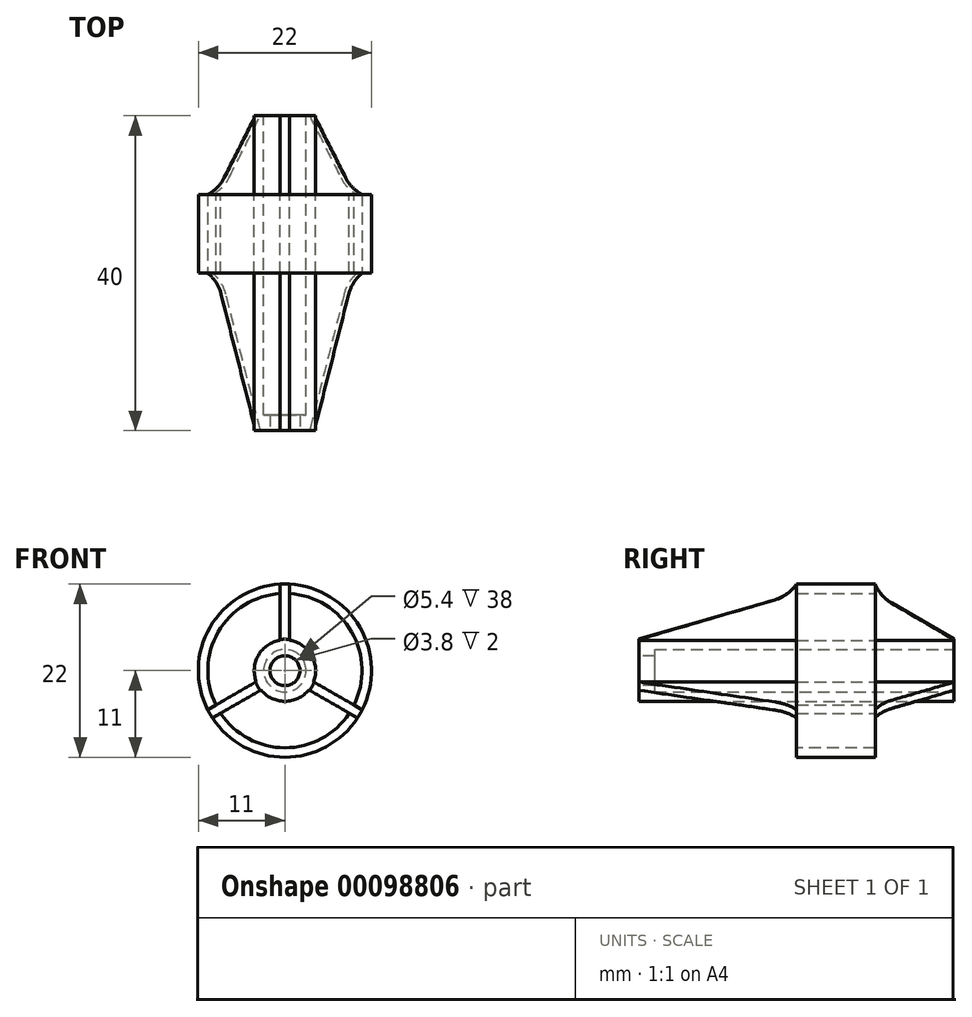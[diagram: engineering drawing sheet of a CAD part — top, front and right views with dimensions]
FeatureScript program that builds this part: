
annotation { "Feature Type Name" : "Feature", "Feature Type Description" : "" }
export const myFeature = defineFeature(function(context is Context, id is Id, definition is map)
    precondition{}
    {
        {
            var Q0;
            Q0=qCreatedBy(makeId("Front.planeOp"),FACE);
            var sketch = newSketch(context, id + "F0", { "sketchPlane" : qUnion([Q0])});
            skCircle(sketch, "E0", {"center": v(0, 0) * mm, "radius": 11 * mm});
            skCircle(sketch, "E1", {"center": v(0, 0) * mm, "radius": 9.8 * mm});
            skCircle(sketch, "E2", {"center": v(0, 0) * mm, "radius": 3.9 * mm});
            skCircle(sketch, "E3", {"center": v(0, 0) * mm, "radius": 2.7 * mm});
            skLineSegment(sketch, "E4", {"start": v(0, 3.9) * mm, "end": v(0, 9.8) * mm, "construction": true});
            skLineSegment(sketch, "E5", {"start": v(3.9, 0) * mm, "end": v(9.8, 0) * mm, "construction": true});
            skLineSegment(sketch, "E6", {"start": v(0, -3.9) * mm, "end": v(0, -9.8) * mm, "construction": true});
            skLineSegment(sketch, "E7", {"start": v(-3.9, 0) * mm, "end": v(-9.8, 0) * mm, "construction": true});
            skLineSegment(sketch, "E8", {"start": v(-0.6, 3.85) * mm, "end": v(-0.6, 9.78) * mm});
            skLineSegment(sketch, "E9", {"start": v(0.6, 9.78) * mm, "end": v(0.6, 3.85) * mm});
            skLineSegment(sketch, "E10.1.0", {"start": v(-8.77, -4.37) * mm, "end": v(-3.64, -1.4) * mm});
            skLineSegment(sketch, "E10.1.1", {"start": v(-3.04, -2.45) * mm, "end": v(-8.17, -5.41) * mm});
            skLineSegment(sketch, "E10.2.0", {"start": v(8.17, -5.41) * mm, "end": v(3.04, -2.45) * mm});
            skLineSegment(sketch, "E10.2.1", {"start": v(3.64, -1.4) * mm, "end": v(8.77, -4.37) * mm});
            skSolve(sketch);
        }
        {
            var Q0;
            Q0=makeQuery(id+"F0.imprint","IMPRINT",FACE,{"disambiguationData":[TD([[makeQuery(id+"F0.imprint","IMPRINT",EDGE,{"derivedFrom":sQuery(id+"F0.wireOp",EDGE,"E0")}),1.0]])]});
            extrude(context, id + "F1", {"entities" : qUnion([Q0]), "oppositeDirection" : true, "depth" : 10 * mm});
        }
        {
            var Q0;
            Q0=makeQuery(id+"F0.imprint","IMPRINT",FACE,{"disambiguationData":[TD([[makeQuery(id+"F0.imprint","IMPRINT",EDGE,{"derivedFrom":sQuery(id+"F0.wireOp",EDGE,"E2")}),1.0]])]});
            extrude(context, id + "F2", {"entities" : qUnion([Q0]), "operationType" : NewBodyOperationType.ADD, "depth" : 20 * mm, "hasSecondDirection" : true, "secondDirectionOppositeDirection" : true, "secondDirectionDepth" : 20 * mm});
        }
        {
            var Q0;
            {var subQ0=sQuery(id+"F0.wireOp",EDGE,"E8");Q0=makeQuery(id+"F0.imprint","IMPRINT",FACE,{"disambiguationData":[TD([[makeQuery(id+"F0.imprint","IMPRINT",EDGE,{"derivedFrom":subQ0}),-1.0]])]});}
            var Q1;
            {var subQ0=sQuery(id+"F0.wireOp",EDGE,"E10.2.0");Q1=makeQuery(id+"F0.imprint","IMPRINT",FACE,{"disambiguationData":[TD([[makeQuery(id+"F0.imprint","IMPRINT",EDGE,{"derivedFrom":subQ0}),-1.0]])]});}
            var Q2;
            {var subQ0=sQuery(id+"F0.wireOp",EDGE,"E10.1.0");Q2=makeQuery(id+"F0.imprint","IMPRINT",FACE,{"disambiguationData":[TD([[makeQuery(id+"F0.imprint","IMPRINT",EDGE,{"derivedFrom":subQ0}),-1.0]])]});}
            extrude(context, id + "F3", {"entities" : qUnion([Q0, Q1, Q2]), "operationType" : NewBodyOperationType.ADD, "depth" : 20 * mm, "hasSecondDirection" : true, "secondDirectionOppositeDirection" : true, "secondDirectionDepth" : 20 * mm});
        }
        {
            var Q0;
            {var subQ0=sQuery(id+"F0.wireOp",EDGE,"E2");var subQ1=sQuery(id+"F0.wireOp",EDGE,"E1");Q0=makeQuery(id+"F3.boolean.opBoolean","MERGE",FACE,{"derivedFrom":[makeQuery(id+"F2.opExtrude","CAP_FACE",FACE,{"disambiguationData":[OSD([subQ0,sQuery(id+"F0.wireOp",EDGE,"E3")])],"isStart":false}),makeQuery(id+"F3.opExtrude","CAP_FACE",FACE,{"disambiguationData":[OSD([subQ1,subQ0,sQuery(id+"F0.wireOp",EDGE,"d82addfd-7540-4472-8b44-bfc7bcca903d0.MirrorCS"),sQuery(id+"F0.wireOp",EDGE,"ad947069-a3ec-42d5-bcbd-703db36c13fa.trimOffspring")])],"isStart":false}),makeQuery(id+"F3.opExtrude","CAP_FACE",FACE,{"disambiguationData":[OSD([subQ1,subQ0,sQuery(id+"F0.wireOp",EDGE,"70a96751-7a45-4760-83c1-48eb2839d5d3.1.0"),sQuery(id+"F0.wireOp",EDGE,"70a96751-7a45-4760-83c1-48eb2839d5d3.1.1")])],"isStart":false}),makeQuery(id+"F3.opExtrude","CAP_FACE",FACE,{"disambiguationData":[OSD([subQ1,subQ0,sQuery(id+"F0.wireOp",EDGE,"70a96751-7a45-4760-83c1-48eb2839d5d3.2.0"),sQuery(id+"F0.wireOp",EDGE,"70a96751-7a45-4760-83c1-48eb2839d5d3.2.1")])],"isStart":false})]});}
            var sketch = newSketch(context, id + "F4", { "sketchPlane" : qUnion([Q0])});
            skCircle(sketch, "E11", {"center": v(0, 0) * mm, "radius": 1.9 * mm});
            skSolve(sketch);
        }
        {
            var Q0;
            Q0=makeQuery(id+"F4.imprint","IMPRINT",FACE,{"disambiguationData":[TD([[makeQuery(id+"F4.imprint","IMPRINT",EDGE,{"derivedFrom":sQuery(id+"F4.wireOp",EDGE,"E11")}),-1.0]])]});
            extrude(context, id + "F5", {"entities" : qUnion([Q0]), "operationType" : NewBodyOperationType.ADD, "oppositeDirection" : true, "depth" : 2 * mm});
        }
        {
            var Q0;
            {var subQ0=sQuery(id+"F0.wireOp",EDGE,"E1");Q0=makeQuery(id+"F3.opExtrude","CAP_EDGE",EDGE,{"disambiguationData":[OSD([subQ0]),TDD([makeQuery(id+"F0.imprint","IMPRINT",EDGE,{"disambiguationData":[TD([[makeQuery(id+"F0.imprint","INTERSECT",VERTEX,{"derivedFrom":[subQ0,sQuery(id+"F0.wireOp",EDGE,"E8")]}),1.0]])],"derivedFrom":subQ0})])],"isStart":false});}
            var Q1;
            {var subQ0=sQuery(id+"F0.wireOp",EDGE,"E1");Q1=makeQuery(id+"F3.opExtrude","CAP_EDGE",EDGE,{"disambiguationData":[OSD([subQ0]),TDD([makeQuery(id+"F0.imprint","IMPRINT",EDGE,{"disambiguationData":[TD([[makeQuery(id+"F0.imprint","INTERSECT",VERTEX,{"derivedFrom":[subQ0,sQuery(id+"F0.wireOp",EDGE,"E10.1.0")]}),-1.0]])],"derivedFrom":subQ0})])],"isStart":false});}
            var Q2;
            {var subQ0=sQuery(id+"F0.wireOp",EDGE,"E1");Q2=makeQuery(id+"F3.opExtrude","CAP_EDGE",EDGE,{"disambiguationData":[OSD([subQ0]),TDD([makeQuery(id+"F0.imprint","IMPRINT",EDGE,{"disambiguationData":[TD([[makeQuery(id+"F0.imprint","INTERSECT",VERTEX,{"derivedFrom":[subQ0,sQuery(id+"F0.wireOp",EDGE,"E10.2.0")]}),-1.0]])],"derivedFrom":subQ0})])],"isStart":false});}
            chamfer(context, id + "F6", {"entities" : qUnion([Q0, Q1, Q2]), "chamferType" : ChamferType.TWO_OFFSETS, "width1" : 5.8 * mm, "oppositeDirection" : false, "width2" : 20 * mm, "tangentPropagation" : true});
        }
        {
            var Q0;
            {var subQ0=sQuery(id+"F0.wireOp",EDGE,"E1");Q0=makeQuery(id+"F3.opExtrude","CAP_EDGE",EDGE,{"disambiguationData":[OSD([subQ0]),TDD([makeQuery(id+"F0.imprint","IMPRINT",EDGE,{"disambiguationData":[TD([[makeQuery(id+"F0.imprint","INTERSECT",VERTEX,{"derivedFrom":[subQ0,sQuery(id+"F0.wireOp",EDGE,"E10.2.0")]}),-1.0]])],"derivedFrom":subQ0})])],"isStart":true});}
            var Q1;
            {var subQ0=sQuery(id+"F0.wireOp",EDGE,"E1");Q1=makeQuery(id+"F3.opExtrude","CAP_EDGE",EDGE,{"disambiguationData":[OSD([subQ0]),TDD([makeQuery(id+"F0.imprint","IMPRINT",EDGE,{"disambiguationData":[TD([[makeQuery(id+"F0.imprint","INTERSECT",VERTEX,{"derivedFrom":[subQ0,sQuery(id+"F0.wireOp",EDGE,"E10.1.0")]}),-1.0]])],"derivedFrom":subQ0})])],"isStart":true});}
            var Q2;
            {var subQ0=sQuery(id+"F0.wireOp",EDGE,"E1");Q2=makeQuery(id+"F3.opExtrude","CAP_EDGE",EDGE,{"disambiguationData":[OSD([subQ0]),TDD([makeQuery(id+"F0.imprint","IMPRINT",EDGE,{"disambiguationData":[TD([[makeQuery(id+"F0.imprint","INTERSECT",VERTEX,{"derivedFrom":[subQ0,sQuery(id+"F0.wireOp",EDGE,"E8")]}),1.0]])],"derivedFrom":subQ0})])],"isStart":true});}
            chamfer(context, id + "F7", {"entities" : qUnion([Q0, Q1, Q2]), "chamferType" : ChamferType.TWO_OFFSETS, "width1" : 10 * mm, "oppositeDirection" : false, "width2" : 5.8 * mm, "tangentPropagation" : true});
        }
        {
            var Q0;
            {var subQ0=sQuery(id+"F0.wireOp",EDGE,"E1");Q0=makeQuery(id+"F6.opChamfer","BLEND_EDGE",EDGE,{"blendedFrom":[makeQuery(id+"F3.opExtrude","CAP_EDGE",EDGE,{"disambiguationData":[OSD([subQ0]),TDD([makeQuery(id+"F0.imprint","IMPRINT",EDGE,{"disambiguationData":[TD([[makeQuery(id+"F0.imprint","INTERSECT",VERTEX,{"derivedFrom":[subQ0,sQuery(id+"F0.wireOp",EDGE,"E8")]}),1.0]])],"derivedFrom":subQ0})])],"isStart":false}),makeQuery(id+"F1.opExtrude","CAP_FACE",FACE,{"disambiguationData":[OSD([sQuery(id+"F0.wireOp",EDGE,"E0"),subQ0])],"isStart":true})],"blendedInto":[makeQuery(id+"F1.opExtrude","CAP_FACE",FACE,{"disambiguationData":[OSD([sQuery(id+"F0.wireOp",EDGE,"E0"),subQ0])],"isStart":true})]});}
            var Q1;
            {var subQ0=sQuery(id+"F0.wireOp",EDGE,"E1");Q1=makeQuery(id+"F6.opChamfer","BLEND_EDGE",EDGE,{"blendedFrom":[makeQuery(id+"F3.opExtrude","CAP_EDGE",EDGE,{"disambiguationData":[OSD([subQ0]),TDD([makeQuery(id+"F0.imprint","IMPRINT",EDGE,{"disambiguationData":[TD([[makeQuery(id+"F0.imprint","INTERSECT",VERTEX,{"derivedFrom":[subQ0,sQuery(id+"F0.wireOp",EDGE,"E10.2.0")]}),-1.0]])],"derivedFrom":subQ0})])],"isStart":false}),makeQuery(id+"F1.opExtrude","CAP_FACE",FACE,{"disambiguationData":[OSD([sQuery(id+"F0.wireOp",EDGE,"E0"),subQ0])],"isStart":true})],"blendedInto":[makeQuery(id+"F1.opExtrude","CAP_FACE",FACE,{"disambiguationData":[OSD([sQuery(id+"F0.wireOp",EDGE,"E0"),subQ0])],"isStart":true})]});}
            var Q2;
            {var subQ0=sQuery(id+"F0.wireOp",EDGE,"E1");Q2=makeQuery(id+"F6.opChamfer","BLEND_EDGE",EDGE,{"blendedFrom":[makeQuery(id+"F3.opExtrude","CAP_EDGE",EDGE,{"disambiguationData":[OSD([subQ0]),TDD([makeQuery(id+"F0.imprint","IMPRINT",EDGE,{"disambiguationData":[TD([[makeQuery(id+"F0.imprint","INTERSECT",VERTEX,{"derivedFrom":[subQ0,sQuery(id+"F0.wireOp",EDGE,"E10.1.0")]}),-1.0]])],"derivedFrom":subQ0})])],"isStart":false}),makeQuery(id+"F1.opExtrude","CAP_FACE",FACE,{"disambiguationData":[OSD([sQuery(id+"F0.wireOp",EDGE,"E0"),subQ0])],"isStart":true})],"blendedInto":[makeQuery(id+"F1.opExtrude","CAP_FACE",FACE,{"disambiguationData":[OSD([sQuery(id+"F0.wireOp",EDGE,"E0"),subQ0])],"isStart":true})]});}
            fillet(context, id + "F8", {"entities" : qUnion([Q0, Q1, Q2]), "radius" : 5 * mm, "tangentPropagation" : true, "allowEdgeOverflow" : false});
        }
        {
            var Q0;
            {var subQ0=sQuery(id+"F0.wireOp",EDGE,"E1");Q0=makeQuery(id+"F7.opChamfer","BLEND_EDGE",EDGE,{"blendedFrom":[makeQuery(id+"F3.opExtrude","CAP_EDGE",EDGE,{"disambiguationData":[OSD([subQ0]),TDD([makeQuery(id+"F0.imprint","IMPRINT",EDGE,{"disambiguationData":[TD([[makeQuery(id+"F0.imprint","INTERSECT",VERTEX,{"derivedFrom":[subQ0,sQuery(id+"F0.wireOp",EDGE,"E10.2.0")]}),-1.0]])],"derivedFrom":subQ0})])],"isStart":true}),makeQuery(id+"F1.opExtrude","CAP_FACE",FACE,{"disambiguationData":[OSD([sQuery(id+"F0.wireOp",EDGE,"E0"),subQ0])],"isStart":false})],"blendedInto":[makeQuery(id+"F1.opExtrude","CAP_FACE",FACE,{"disambiguationData":[OSD([sQuery(id+"F0.wireOp",EDGE,"E0"),subQ0])],"isStart":false})]});}
            var Q1;
            {var subQ0=sQuery(id+"F0.wireOp",EDGE,"E1");Q1=makeQuery(id+"F7.opChamfer","BLEND_EDGE",EDGE,{"blendedFrom":[makeQuery(id+"F3.opExtrude","CAP_EDGE",EDGE,{"disambiguationData":[OSD([subQ0]),TDD([makeQuery(id+"F0.imprint","IMPRINT",EDGE,{"disambiguationData":[TD([[makeQuery(id+"F0.imprint","INTERSECT",VERTEX,{"derivedFrom":[subQ0,sQuery(id+"F0.wireOp",EDGE,"E10.1.0")]}),-1.0]])],"derivedFrom":subQ0})])],"isStart":true}),makeQuery(id+"F1.opExtrude","CAP_FACE",FACE,{"disambiguationData":[OSD([sQuery(id+"F0.wireOp",EDGE,"E0"),subQ0])],"isStart":false})],"blendedInto":[makeQuery(id+"F1.opExtrude","CAP_FACE",FACE,{"disambiguationData":[OSD([sQuery(id+"F0.wireOp",EDGE,"E0"),subQ0])],"isStart":false})]});}
            var Q2;
            {var subQ0=sQuery(id+"F0.wireOp",EDGE,"E1");Q2=makeQuery(id+"F7.opChamfer","BLEND_EDGE",EDGE,{"blendedFrom":[makeQuery(id+"F3.opExtrude","CAP_EDGE",EDGE,{"disambiguationData":[OSD([subQ0]),TDD([makeQuery(id+"F0.imprint","IMPRINT",EDGE,{"disambiguationData":[TD([[makeQuery(id+"F0.imprint","INTERSECT",VERTEX,{"derivedFrom":[subQ0,sQuery(id+"F0.wireOp",EDGE,"E8")]}),1.0]])],"derivedFrom":subQ0})])],"isStart":true}),makeQuery(id+"F1.opExtrude","CAP_FACE",FACE,{"disambiguationData":[OSD([sQuery(id+"F0.wireOp",EDGE,"E0"),subQ0])],"isStart":false})],"blendedInto":[makeQuery(id+"F1.opExtrude","CAP_FACE",FACE,{"disambiguationData":[OSD([sQuery(id+"F0.wireOp",EDGE,"E0"),subQ0])],"isStart":false})]});}
            fillet(context, id + "F9", {"entities" : qUnion([Q0, Q1, Q2]), "radius" : 5 * mm, "tangentPropagation" : true, "allowEdgeOverflow" : false});
        }
    });
